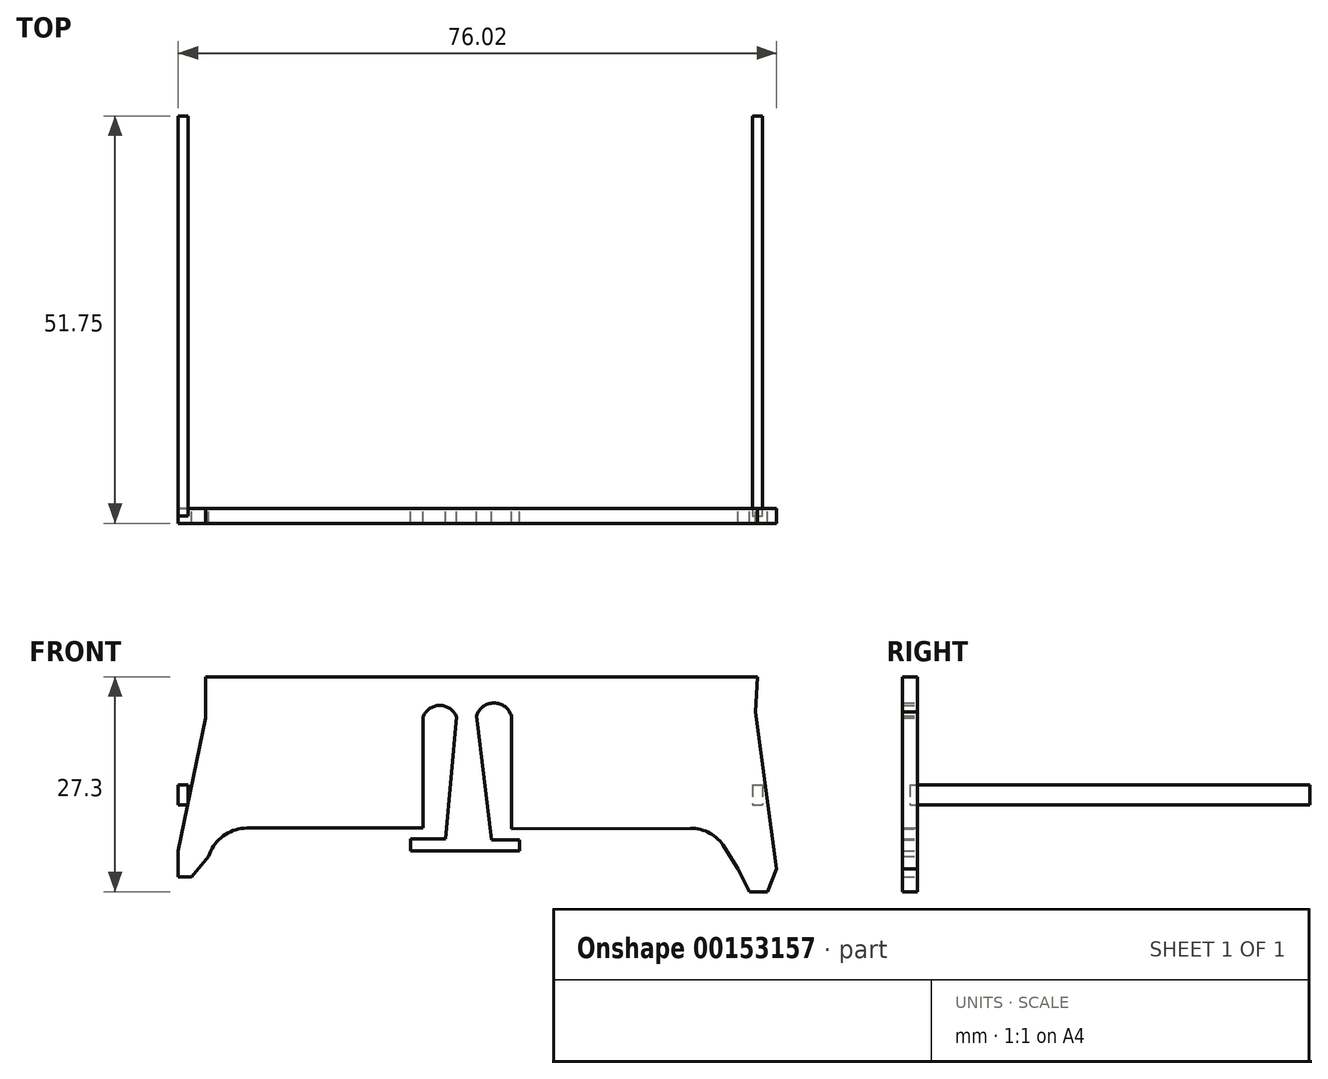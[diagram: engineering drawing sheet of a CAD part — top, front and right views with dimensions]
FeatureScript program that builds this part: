
annotation { "Feature Type Name" : "Feature", "Feature Type Description" : "" }
export const myFeature = defineFeature(function(context is Context, id is Id, definition is map)
    precondition{}
    {
        {
            var Q0;
            Q0=qCreatedBy(makeId("Front.planeOp"),FACE);
            var sketch = newSketch(context, id + "F0", { "sketchPlane" : qUnion([Q0])});
            skLineSegment(sketch, "E0", {"start": v(-54.16, 15.04) * mm, "end": v(-54.16, 9.78) * mm});
            skLineSegment(sketch, "E1", {"start": v(-54.16, 9.78) * mm, "end": v(-57.65, -7.06) * mm});
            skLineSegment(sketch, "E2", {"start": v(-57.65, -7.06) * mm, "end": v(-57.65, -10.4) * mm});
            skLineSegment(sketch, "E3", {"start": v(-57.65, -10.4) * mm, "end": v(-55.97, -10.4) * mm});
            skLineSegment(sketch, "E4", {"start": v(-55.97, -10.4) * mm, "end": v(-53.82, -7.77) * mm});
            skLineSegment(sketch, "E5", {"start": v(-53.82, -7.77) * mm, "end": v(-52.14, -4.19) * mm});
            skLineSegment(sketch, "E6", {"start": v(-52.14, -4.19) * mm, "end": v(-26.55, -4.19) * mm});
            skLineSegment(sketch, "E7", {"start": v(-26.55, -4.19) * mm, "end": v(-26.55, 9.93) * mm});
            skLineSegment(sketch, "E8", {"start": v(-22.3, 9.93) * mm, "end": v(-23.7, -5.55) * mm});
            skLineSegment(sketch, "E9", {"start": v(-23.7, -5.55) * mm, "end": v(-28.13, -5.55) * mm});
            skLineSegment(sketch, "E10", {"start": v(-28.13, -5.55) * mm, "end": v(-28.13, -7.07) * mm});
            skLineSegment(sketch, "E11", {"start": v(-54.16, 15.04) * mm, "end": v(15.9, 15.04) * mm});
            skLineSegment(sketch, "E12", {"start": v(18.37, -9.35) * mm, "end": v(17.23, -12.26) * mm});
            skLineSegment(sketch, "E13", {"start": v(17.23, -12.26) * mm, "end": v(14.95, -12.26) * mm});
            skLineSegment(sketch, "E14", {"start": v(14.95, -12.26) * mm, "end": v(13.43, -9.35) * mm});
            skLineSegment(sketch, "E15", {"start": v(13.43, -9.35) * mm, "end": v(10.26, -4.19) * mm});
            skLineSegment(sketch, "E16", {"start": v(-28.13, -7.07) * mm, "end": v(-14.32, -7.07) * mm});
            skLineSegment(sketch, "E17", {"start": v(-14.32, -7.07) * mm, "end": v(-14.32, -5.67) * mm});
            skLineSegment(sketch, "E18", {"start": v(-14.32, -5.67) * mm, "end": v(-17.86, -5.67) * mm});
            skLineSegment(sketch, "E19", {"start": v(-17.86, -5.67) * mm, "end": v(-19.77, 10.04) * mm});
            skLineSegment(sketch, "E20", {"start": v(-15.33, 10.04) * mm, "end": v(-15.33, -4.28) * mm});
            skLineSegment(sketch, "E21", {"start": v(10.26, -4.19) * mm, "end": v(-15.33, -4.28) * mm});
            skLineSegment(sketch, "E22", {"start": v(18.37, -9.35) * mm, "end": v(15.67, 10.56) * mm});
            skLineSegment(sketch, "E23", {"start": v(15.67, 10.56) * mm, "end": v(15.9, 15.04) * mm});
            skArc(sketch, "E24", {"start": v(-22.3, 9.93) * mm, "mid": v(-24.43, 11.4) * mm, "end": v(-26.55, 9.93) * mm});
            skArc(sketch, "E25", {"start": v(-15.33, 10.04) * mm, "mid": v(-17.55, 11.7) * mm, "end": v(-19.77, 10.04) * mm});
            skSolve(sketch);
        }
        {
            var Q0;
            Q0 = qSketchRegion(id + "F0", true);
            extrude(context, id + "F1", {"entities" : qUnion([Q0]), "endBound" : BoundingType.SYMMETRIC, "depth" : 1.9 * mm});
        }
        {
            var Q0;
            Q0=qCreatedBy(makeId("Top.planeOp"),FACE);
            var sketch = newSketch(context, id + "F2", { "sketchPlane" : qUnion([Q0])});
            skLineSegment(sketch, "E26", {"start": v(-57.65, 0) * mm, "end": v(-57.65, 50.8) * mm});
            skLineSegment(sketch, "E27", {"start": v(-57.65, 50.8) * mm, "end": v(-56.38, 50.8) * mm});
            skLineSegment(sketch, "E28", {"start": v(-56.38, 50.8) * mm, "end": v(-56.38, 0) * mm});
            skLineSegment(sketch, "E29", {"start": v(-56.38, 0) * mm, "end": v(-57.65, 0) * mm});
            skLineSegment(sketch, "E30", {"start": v(16.58, 0) * mm, "end": v(16.58, 50.8) * mm});
            skLineSegment(sketch, "E31", {"start": v(16.58, 50.8) * mm, "end": v(15.3, 50.8) * mm});
            skLineSegment(sketch, "E32", {"start": v(15.3, 50.8) * mm, "end": v(15.3, 0) * mm});
            skLineSegment(sketch, "E33", {"start": v(15.3, 0) * mm, "end": v(16.58, 0) * mm});
            skSolve(sketch);
        }
        {
            var Q0;
            Q0 = qSketchRegion(id + "F2", true);
            extrude(context, id + "F3", {"entities" : qUnion([Q0]), "endBound" : BoundingType.SYMMETRIC, "depth" : 2.54 * mm});
        }
        {
            var Q0;
            Q0=makeQuery(id+"F1.opExtrude","SWEPT_EDGE",EDGE,{"disambiguationData":[OSD([sQuery(id+"F0.wireOp",EDGE,"E5"),sQuery(id+"F0.wireOp",EDGE,"E6")])]});
            var Q1;
            Q1=makeQuery(id+"F1.opExtrude","SWEPT_EDGE",EDGE,{"disambiguationData":[OSD([sQuery(id+"F0.wireOp",EDGE,"E15"),sQuery(id+"F0.wireOp",EDGE,"E21")])]});
            fillet(context, id + "F4", {"entities" : qUnion([Q0, Q1]), "radius" : 5.08 * mm, "tangentPropagation" : true, "allowEdgeOverflow" : false});
        }
    });
